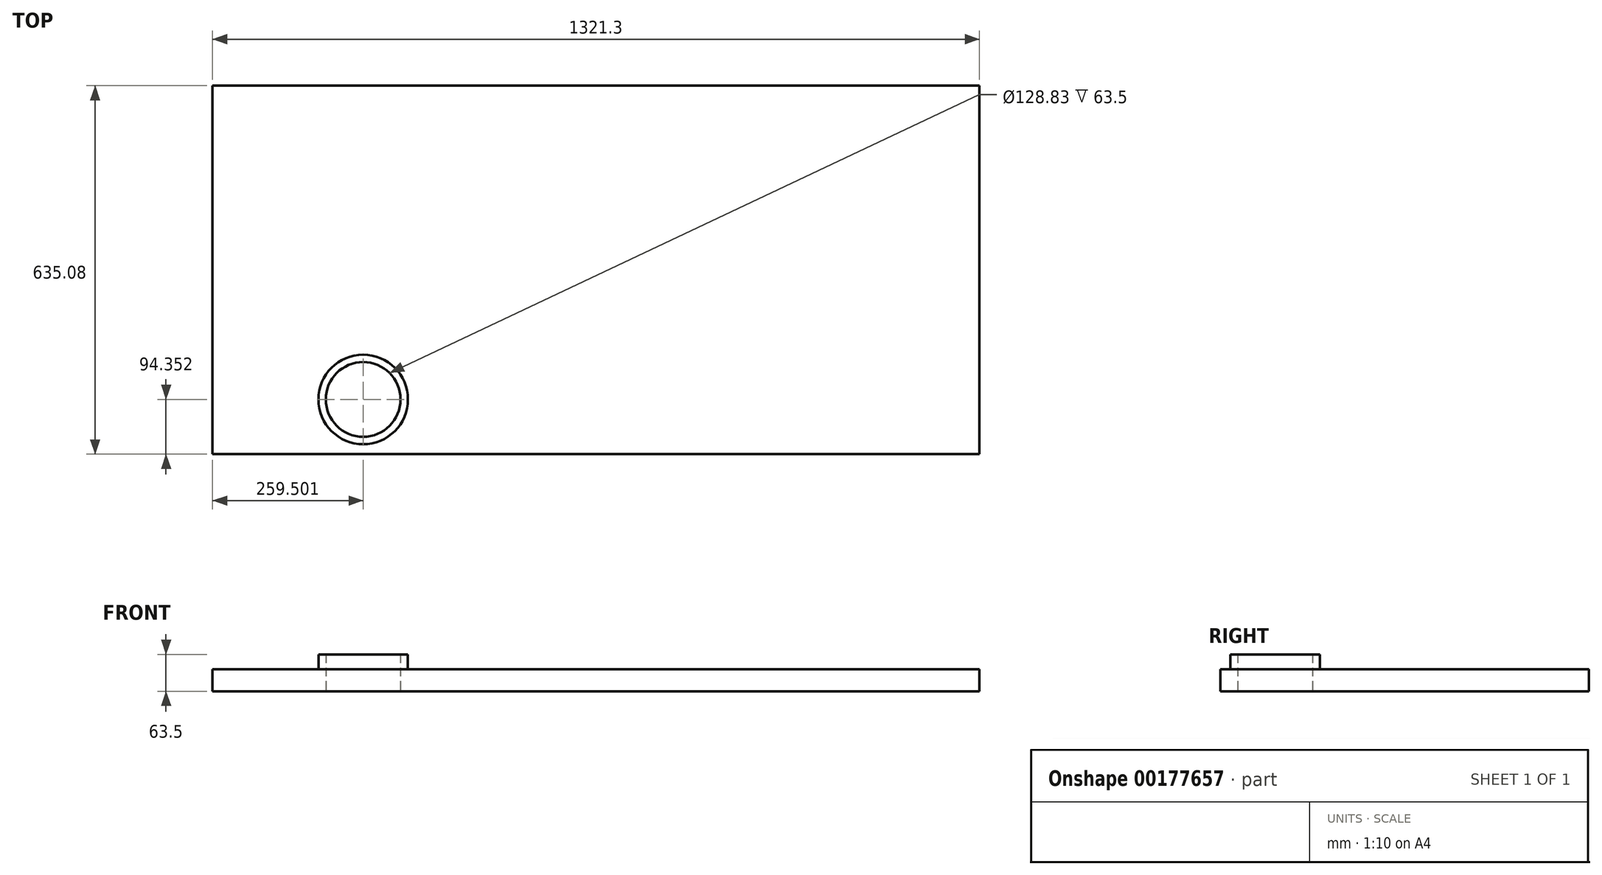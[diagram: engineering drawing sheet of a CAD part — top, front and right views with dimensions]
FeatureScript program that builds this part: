
annotation { "Feature Type Name" : "Feature", "Feature Type Description" : "" }
export const myFeature = defineFeature(function(context is Context, id is Id, definition is map)
    precondition{}
    {
        {
            var Q0;
            Q0=qCreatedBy(makeId("Top.planeOp"),FACE);
            var sketch = newSketch(context, id + "F0", { "sketchPlane" : qUnion([Q0])});
            skLineSegment(sketch, "E0.bottom", {"start": v(-660.65, 317.54) * mm, "end": v(660.65, 317.54) * mm});
            skLineSegment(sketch, "E0.top", {"start": v(-660.65, -317.54) * mm, "end": v(660.65, -317.54) * mm});
            skLineSegment(sketch, "E0.left", {"start": v(-660.65, 317.54) * mm, "end": v(-660.65, -317.54) * mm});
            skLineSegment(sketch, "E0.right", {"start": v(660.65, 317.54) * mm, "end": v(660.65, -317.54) * mm});
            skPoint(sketch, "E0.middle", {"position": v(0, 0) * mm});
            skCircle(sketch, "E1", {"center": v(-401.15, -223.19) * mm, "radius": 64.41 * mm});
            skSolve(sketch);
        }
        {
            var Q0;
            Q0 = qSketchRegion(id + "F0", true);
            extrude(context, id + "F1", {"entities" : qUnion([Q0]), "depth" : 38.1 * mm});
        }
        {
            var Q0;
            Q0=makeQuery(id+"F1.opExtrude","CAP_FACE",FACE,{"disambiguationData":[OSD([sQuery(id+"F0.wireOp",EDGE,"E0.bottom"),sQuery(id+"F0.wireOp",EDGE,"E0.top"),sQuery(id+"F0.wireOp",EDGE,"E0.left"),sQuery(id+"F0.wireOp",EDGE,"E0.right"),sQuery(id+"F0.wireOp",EDGE,"E1")])],"isStart":false});
            var sketch = newSketch(context, id + "F2", { "sketchPlane" : qUnion([Q0])});
            skCircle(sketch, "E2.0", {"center": v(-401.15, -223.19) * mm, "radius": 77.11 * mm});
            skSolve(sketch);
        }
        {
            var Q0;
            Q0=makeQuery(id+"F2.imprint","IMPRINT",FACE,{"disambiguationData":[TD([[makeQuery(id+"F2.imprint","IMPRINT",EDGE,{"derivedFrom":sQuery(id+"F2.wireOp",EDGE,"E2.0")}),1.0]])]});
            extrude(context, id + "F3", {"entities" : qUnion([Q0]), "operationType" : NewBodyOperationType.ADD, "depth" : 25.4 * mm});
        }
    });
